# Revit family: Bathtub-Recessed-American_Standard-New_Salem-0255_Series
name_source: partatom
category: Plumbing Fixtures
revit_build: Autodesk Revit 2014 (Build: 20130308_1515(x64)
units: mm (PartAtom-declared; Revit-internal decimal feet)

## types (1)
- 0255.112
    ADA Compliant = Yes
    CW Connection = No
    Default Elevation = 0"
    Description = New Salem Recess Bath Enameled Steel.
    HW Connection = No
    Height = 14 1/4"
    Installation Type = Floor Mounted
    Length = 60"
    Manufacturer = American Standard
    Material = Vitreous China-American Standard-020-White
    Model = 0255.112
    Price = Prices may vary. Please consult Manufacturer Representative for most up-to-date price list.
    Product Documentation Link = http://www.americanstandard-us.com
    Product Page URL = http://www.americanstandard-us.com
    Shipping Weight = 80 lb
    URL = http://www.americanstandard-us.com
    Vent Connection = No
    Warranty Information = 1 Year (Limited)
    Waste Connection = Yes
    Waste Connection Diameter = 1 1/2"
    Width = 30"

## geometry (parser evidence)
native form markers: Sweep x1
no freeform markers — native parametric forms only
